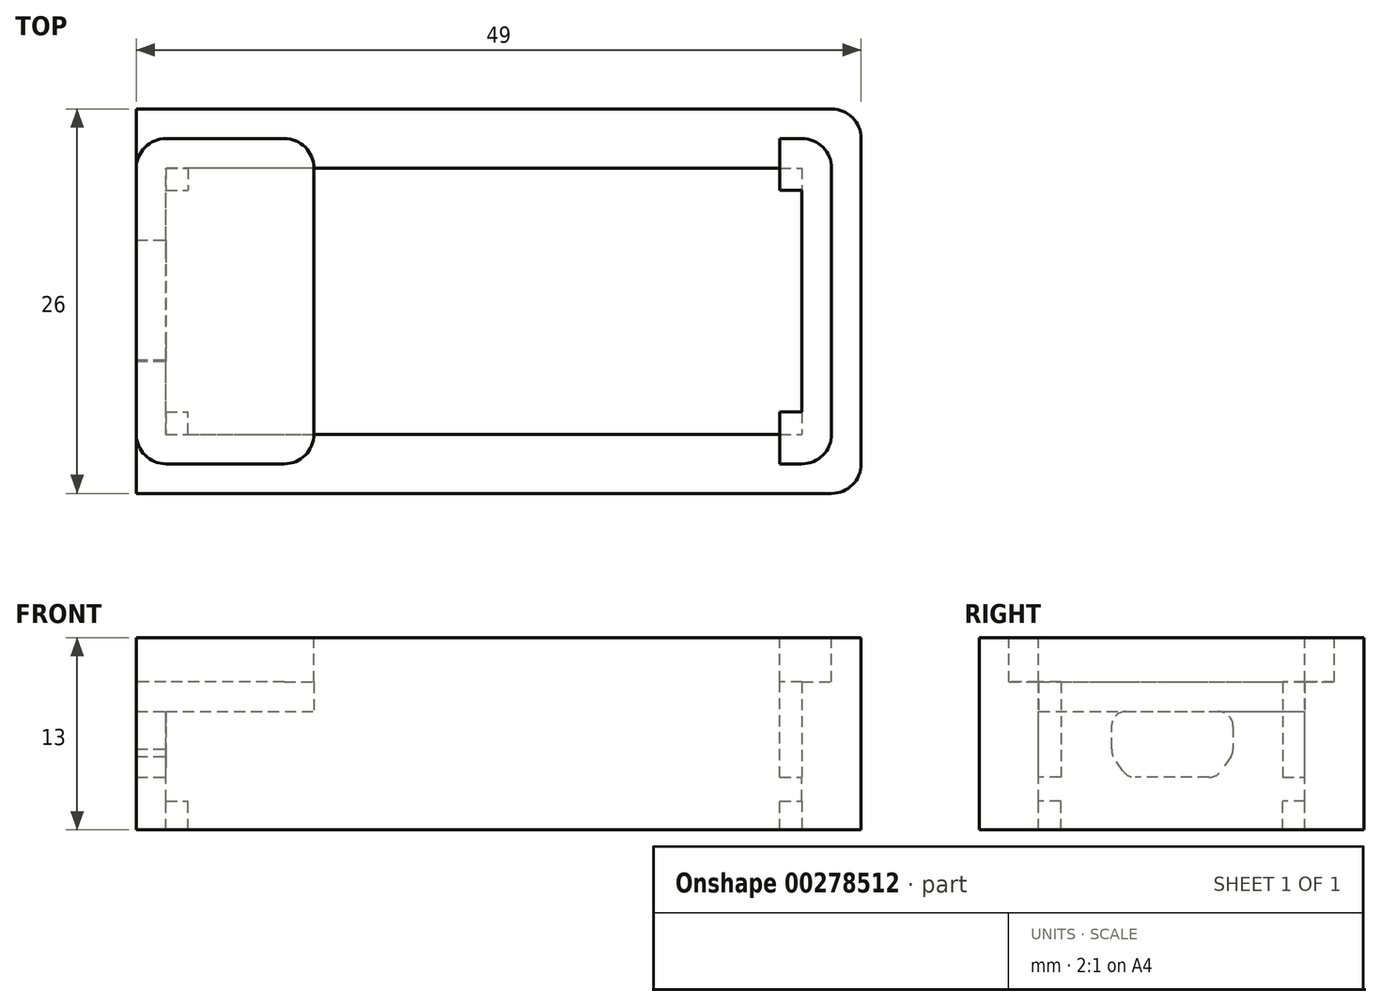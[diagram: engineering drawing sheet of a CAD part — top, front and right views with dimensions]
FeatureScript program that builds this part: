
annotation { "Feature Type Name" : "Feature", "Feature Type Description" : "" }
export const myFeature = defineFeature(function(context is Context, id is Id, definition is map)
    precondition{}
    {
        {
            var Q0;
            Q0=qCreatedBy(makeId("Top.planeOp"),FACE);
            var sketch = newSketch(context, id + "F0", { "sketchPlane" : qUnion([Q0])});
            skLineSegment(sketch, "E0.bottom", {"start": v(-21.5, 9) * mm, "end": v(21.5, 9) * mm, "construction": true});
            skLineSegment(sketch, "E0.top", {"start": v(-21.5, -9) * mm, "end": v(21.5, -9) * mm, "construction": true});
            skLineSegment(sketch, "E0.left", {"start": v(-21.5, 9) * mm, "end": v(-21.5, -9) * mm, "construction": true});
            skLineSegment(sketch, "E0.right", {"start": v(21.5, 9) * mm, "end": v(21.5, -9) * mm, "construction": true});
            skPoint(sketch, "E0.middle", {"position": v(0, 0) * mm});
            skLineSegment(sketch, "E1", {"start": v(-11.5, 15.37) * mm, "end": v(-11.5, -15.55) * mm, "construction": true});
            skLineSegment(sketch, "E2.bottom", {"start": v(-11.5, 9) * mm, "end": v(-21.5, 9) * mm});
            skLineSegment(sketch, "E2.top", {"start": v(-11.5, 11) * mm, "end": v(-21.5, 11) * mm});
            skLineSegment(sketch, "E2.left", {"start": v(-11.5, 9) * mm, "end": v(-11.5, 11) * mm});
            skLineSegment(sketch, "E2.right", {"start": v(-21.5, 9) * mm, "end": v(-21.5, 11) * mm});
            skLineSegment(sketch, "E3.bottom", {"start": v(-21.5, 9) * mm, "end": v(-11.5, 9) * mm});
            skLineSegment(sketch, "E3.top", {"start": v(-21.5, -9) * mm, "end": v(-11.5, -9) * mm});
            skLineSegment(sketch, "E3.left", {"start": v(-21.5, 9) * mm, "end": v(-21.5, -9) * mm});
            skLineSegment(sketch, "E3.right", {"start": v(-11.5, 9) * mm, "end": v(-11.5, -9) * mm});
            skLineSegment(sketch, "E4.MirrorCS", {"start": v(-21.5, -9) * mm, "end": v(-21.5, -11) * mm});
            skLineSegment(sketch, "E5.MirrorCS", {"start": v(-11.5, -11) * mm, "end": v(-21.5, -11) * mm});
            skLineSegment(sketch, "E6.MirrorCS", {"start": v(-11.5, -9) * mm, "end": v(-11.5, -11) * mm});
            skLineSegment(sketch, "E7.bottom", {"start": v(21.5, -9) * mm, "end": v(20, -9) * mm});
            skLineSegment(sketch, "E7.top", {"start": v(21.5, -11) * mm, "end": v(20, -11) * mm});
            skLineSegment(sketch, "E7.left", {"start": v(21.5, -9) * mm, "end": v(21.5, -11) * mm});
            skLineSegment(sketch, "E7.right", {"start": v(20, -9) * mm, "end": v(20, -11) * mm});
            skLineSegment(sketch, "E8.MirrorCS", {"start": v(20, 9) * mm, "end": v(20, 11) * mm});
            skLineSegment(sketch, "E9.MirrorCS", {"start": v(21.5, 11) * mm, "end": v(20, 11) * mm});
            skLineSegment(sketch, "E10.MirrorCS", {"start": v(21.5, 9) * mm, "end": v(21.5, 11) * mm});
            skLineSegment(sketch, "E11", {"start": v(21.5, 9) * mm, "end": v(20, 9) * mm});
            skLineSegment(sketch, "E12.bottom", {"start": v(21.5, -11) * mm, "end": v(23.5, -11) * mm});
            skLineSegment(sketch, "E12.top", {"start": v(21.5, 11) * mm, "end": v(23.5, 11) * mm});
            skLineSegment(sketch, "E12.left", {"start": v(21.5, -11) * mm, "end": v(21.5, 11) * mm});
            skLineSegment(sketch, "E12.right", {"start": v(23.5, -11) * mm, "end": v(23.5, 11) * mm});
            skLineSegment(sketch, "E13.bottom", {"start": v(20, -9) * mm, "end": v(21.5, -9) * mm});
            skLineSegment(sketch, "E13.top", {"start": v(20, -7.5) * mm, "end": v(21.5, -7.5) * mm});
            skLineSegment(sketch, "E13.left", {"start": v(20, -9) * mm, "end": v(20, -7.5) * mm});
            skLineSegment(sketch, "E13.right", {"start": v(21.5, -9) * mm, "end": v(21.5, -7.5) * mm});
            skLineSegment(sketch, "E14.top", {"start": v(21.5, 7.5) * mm, "end": v(20, 7.5) * mm});
            skLineSegment(sketch, "E14.left", {"start": v(21.5, 9) * mm, "end": v(21.5, 7.5) * mm});
            skLineSegment(sketch, "E14.right", {"start": v(20, 9) * mm, "end": v(20, 7.5) * mm});
            skSolve(sketch);
        }
        {
            var Q0;
            {var subQ2=sQuery(id+"F0.wireOp",EDGE,"E11");var subQ3=makeQuery(id+"F0.imprint","IMPRINT",EDGE,{"derivedFrom":subQ2});var subQ4=sQuery(id+"F0.wireOp",EDGE,"E7.left");var subQ5=makeQuery(id+"F0.imprint","IMPRINT",EDGE,{"derivedFrom":subQ4});var subQ11=sQuery(id+"F0.wireOp",EDGE,"E7.bottom");var subQ14=makeQuery(id+"F0.imprint","IMPRINT",EDGE,{"derivedFrom":subQ11});var subQ15=makeQuery(id+"F0.imprint","IMPRINT",EDGE,{"derivedFrom":sQuery(id+"F0.wireOp",EDGE,"E2.bottom")});var subQ16=makeQuery(id+"F0.imprint","IMPRINT",EDGE,{"derivedFrom":sQuery(id+"F0.wireOp",EDGE,"E3.top")});Q0=qUnion([makeQuery(id+"F0.imprint","IMPRINT",FACE,{"disambiguationData":[TD([[subQ15,-1.0]])]}),makeQuery(id+"F0.imprint","IMPRINT",FACE,{"disambiguationData":[TD([[subQ16,-1.0]])]}),makeQuery(id+"F0.imprint","IMPRINT",FACE,{"disambiguationData":[TD([[subQ15,1.0]])]}),makeQuery(id+"F0.imprint","IMPRINT",FACE,{"disambiguationData":[TD([[subQ14,1.0]])]}),makeQuery(id+"F0.imprint","IMPRINT",FACE,{"disambiguationData":[TD([[subQ3,1.0]])]}),makeQuery(id+"F0.imprint","IMPRINT",FACE,{"disambiguationData":[TD([[subQ14,-1.0]])]}),makeQuery(id+"F0.imprint","IMPRINT",FACE,{"disambiguationData":[TD([[subQ5,1.0]])]}),makeQuery(id+"F0.imprint","IMPRINT",FACE,{"disambiguationData":[TD([[makeQuery(id+"F0.imprint","IMPRINT",EDGE,{"derivedFrom":sQuery(id+"F0.wireOp",EDGE,"E8.MirrorCS")}),-1.0]])]})]);}
            extrude(context, id + "F1", {"entities" : qUnion([Q0]), "depth" : 2 * mm});
        }
        {
            var Q0;
            Q0=makeQuery(id+"F0.imprint","IMPRINT",FACE,{"disambiguationData":[TD([[makeQuery(id+"F0.imprint","IMPRINT",EDGE,{"derivedFrom":sQuery(id+"F0.wireOp",EDGE,"E2.bottom")}),-1.0]])]});
            var Q1;
            Q1=makeQuery(id+"F0.imprint","IMPRINT",FACE,{"disambiguationData":[TD([[makeQuery(id+"F0.imprint","IMPRINT",EDGE,{"derivedFrom":sQuery(id+"F0.wireOp",EDGE,"E3.top")}),-1.0]])]});
            extrude(context, id + "F2", {"entities" : qUnion([Q0, Q1]), "operationType" : NewBodyOperationType.ADD, "oppositeDirection" : true, "depth" : 8 * mm});
        }
        {
            var Q0;
            {var subQ0=sQuery(id+"F0.wireOp",EDGE,"E4.MirrorCS");var subQ1=sQuery(id+"F0.wireOp",EDGE,"E2.right");Q0=makeQuery(id+"F2.boolean.opBoolean","MERGE",FACE,{"derivedFrom":[makeQuery(id+"F1.opExtrude","SWEPT_FACE",FACE,{"disambiguationData":[OSD([subQ1,sQuery(id+"F0.wireOp",EDGE,"E3.left"),subQ0])]}),makeQuery(id+"F2.opExtrude","SWEPT_FACE",FACE,{"disambiguationData":[OSD([subQ1])]}),makeQuery(id+"F2.opExtrude","SWEPT_FACE",FACE,{"disambiguationData":[OSD([subQ0])]})]});}
            var sketch = newSketch(context, id + "F3", { "sketchPlane" : qUnion([Q0])});
            skLineSegment(sketch, "E15", {"start": v(-9, -6.04) * mm, "end": v(9, -6.04) * mm});
            skPoint(sketch, "E15.endSnap0", {"position": v(9, -4) * mm});
            skLineSegment(sketch, "E16.bottom", {"start": v(-9, -8) * mm, "end": v(-7.5, -8) * mm});
            skLineSegment(sketch, "E16.top", {"start": v(-9, -6.04) * mm, "end": v(-7.5, -6.04) * mm});
            skLineSegment(sketch, "E16.left", {"start": v(-9, -8) * mm, "end": v(-9, -6.04) * mm});
            skLineSegment(sketch, "E16.right", {"start": v(-7.5, -8) * mm, "end": v(-7.5, -6.04) * mm});
            skLineSegment(sketch, "E17.MirrorCS", {"start": v(7.5, -8) * mm, "end": v(7.5, -6.04) * mm});
            skLineSegment(sketch, "E18.MirrorCS", {"start": v(9, -8) * mm, "end": v(7.5, -8) * mm});
            skLineSegment(sketch, "E19.MirrorCS", {"start": v(9, -8) * mm, "end": v(9, -6.04) * mm});
            skArc(sketch, "E20.0.14", {"start": v(2.48, -4.24) * mm, "mid": v(2.86, -4.15) * mm, "end": v(3.15, -3.9) * mm});
            skLineSegment(sketch, "E20.0.15", {"start": v(3.15, -3.9) * mm, "end": v(3.8, -2.93) * mm});
            skArc(sketch, "E20.0.16", {"start": v(3.8, -2.93) * mm, "mid": v(3.85, -2.74) * mm, "end": v(3.85, -2.54) * mm});
            skLineSegment(sketch, "E20.0.17", {"start": v(3.85, -2.54) * mm, "end": v(3.85, -0.9) * mm});
            skArc(sketch, "E20.0.18", {"start": v(3.85, -0.9) * mm, "mid": v(3.64, -0.4) * mm, "end": v(3.15, -0.2) * mm});
            skLineSegment(sketch, "E20.0.19", {"start": v(3.15, -0.2) * mm, "end": v(-3.15, -0.2) * mm});
            skArc(sketch, "E20.0.20", {"start": v(-3.15, -0.2) * mm, "mid": v(-3.72, -0.43) * mm, "end": v(-3.95, -1) * mm});
            skLineSegment(sketch, "E20.0.21", {"start": v(-3.95, -1) * mm, "end": v(-3.95, -2.54) * mm});
            skArc(sketch, "E20.0.22", {"start": v(-3.95, -2.54) * mm, "mid": v(-3.92, -2.74) * mm, "end": v(-3.83, -2.93) * mm});
            skLineSegment(sketch, "E20.0.23", {"start": v(-3.83, -2.93) * mm, "end": v(-3.18, -3.9) * mm});
            skArc(sketch, "E20.0.24", {"start": v(-3.18, -3.9) * mm, "mid": v(-2.9, -4.15) * mm, "end": v(-2.52, -4.24) * mm});
            skLineSegment(sketch, "E21", {"start": v(-2.52, -4.24) * mm, "end": v(2.48, -4.24) * mm});
            skArc(sketch, "E22.0", {"start": v(3.97, -3.03) * mm, "mid": v(4.05, -2.78) * mm, "end": v(4.05, -2.52) * mm});
            skLineSegment(sketch, "E22.1", {"start": v(-4.15, -1) * mm, "end": v(-4.15, -2.54) * mm});
            skArc(sketch, "E22.2", {"start": v(-3.15, 0) * mm, "mid": v(-3.86, -0.3) * mm, "end": v(-4.15, -1) * mm});
            skLineSegment(sketch, "E22.3", {"start": v(3.15, 0) * mm, "end": v(-3.15, 0) * mm});
            skArc(sketch, "E22.4", {"start": v(4.05, -0.9) * mm, "mid": v(3.79, -0.26) * mm, "end": v(3.15, 0) * mm});
            skArc(sketch, "E22.5", {"start": v(-4.15, -2.54) * mm, "mid": v(-4.11, -2.8) * mm, "end": v(-4, -3.04) * mm});
            skLineSegment(sketch, "E22.6", {"start": v(4.05, -2.52) * mm, "end": v(4.05, -0.9) * mm});
            skLineSegment(sketch, "E22.7", {"start": v(-4, -3.04) * mm, "end": v(-3.35, -4) * mm});
            skArc(sketch, "E22.8", {"start": v(-3.35, -4) * mm, "mid": v(-2.99, -4.33) * mm, "end": v(-2.52, -4.44) * mm});
            skLineSegment(sketch, "E22.9", {"start": v(-2.52, -4.44) * mm, "end": v(2.48, -4.44) * mm});
            skArc(sketch, "E22.10", {"start": v(2.48, -4.44) * mm, "mid": v(2.95, -4.33) * mm, "end": v(3.31, -4) * mm});
            skLineSegment(sketch, "E22.11", {"start": v(3.31, -4) * mm, "end": v(3.97, -3.03) * mm});
            skPoint(sketch, "E23", {"position": v(0, 0) * mm});
            skLineSegment(sketch, "E24", {"start": v(7.5, -8) * mm, "end": v(-7.5, -8) * mm});
            skSolve(sketch);
        }
        {
            var Q0;
            Q0=makeQuery(id+"F3.imprint","IMPRINT",FACE,{"disambiguationData":[TD([[makeQuery(id+"F3.imprint","IMPRINT",EDGE,{"derivedFrom":sQuery(id+"F3.wireOp",EDGE,"E22.0")}),-1.0]])]});
            var Q1;
            {var subQ10=sQuery(id+"F3.wireOp",EDGE,"E16.left");Q1=makeQuery(id+"F3.imprint","IMPRINT",FACE,{"disambiguationData":[TD([[makeQuery(id+"F3.imprint","IMPRINT",EDGE,{"derivedFrom":subQ10}),1.0]])]});}
            var Q2;
            {var subQ0=sQuery(id+"F3.wireOp",EDGE,"E16.right");Q2=makeQuery(id+"F3.imprint","IMPRINT",FACE,{"disambiguationData":[TD([[makeQuery(id+"F3.imprint","IMPRINT",EDGE,{"derivedFrom":subQ0}),-1.0]])]});}
            extrude(context, id + "F4", {"entities" : qUnion([Q0, Q1, Q2]), "operationType" : NewBodyOperationType.ADD, "depth" : 2 * mm});
        }
        {
            var Q0;
            {var subQ0=sQuery(id+"F3.wireOp",EDGE,"E17.MirrorCS");Q0=makeQuery(id+"F3.imprint","IMPRINT",FACE,{"disambiguationData":[TD([[makeQuery(id+"F3.imprint","IMPRINT",EDGE,{"derivedFrom":subQ0}),-1.0]])]});}
            var Q1;
            Q1=makeQuery(id+"F3.imprint","IMPRINT",FACE,{"disambiguationData":[TD([[makeQuery(id+"F3.imprint","IMPRINT",EDGE,{"derivedFrom":sQuery(id+"F3.wireOp",EDGE,"E16.bottom")}),1.0]])]});
            var Q2;
            Q2=makeQuery(id+"F4.opExtrude","CAP_FACE",FACE,{"disambiguationData":[OSD([sQuery(id+"F0.wireOp",EDGE,"E2.top"),sQuery(id+"F0.wireOp",EDGE,"E2.right"),sQuery(id+"F0.wireOp",EDGE,"E3.left"),sQuery(id+"F0.wireOp",EDGE,"E4.MirrorCS"),sQuery(id+"F0.wireOp",EDGE,"E5.MirrorCS"),sQuery(id+"F3.wireOp",EDGE,"E15"),sQuery(id+"F3.wireOp",EDGE,"E16.left"),sQuery(id+"F3.wireOp",EDGE,"E16.right"),sQuery(id+"F3.wireOp",EDGE,"E17.MirrorCS"),sQuery(id+"F3.wireOp",EDGE,"E19.MirrorCS"),sQuery(id+"F3.wireOp",EDGE,"E22.0"),sQuery(id+"F3.wireOp",EDGE,"E22.1"),sQuery(id+"F3.wireOp",EDGE,"E22.2"),sQuery(id+"F3.wireOp",EDGE,"E22.3"),sQuery(id+"F3.wireOp",EDGE,"E22.4"),sQuery(id+"F3.wireOp",EDGE,"E22.5"),sQuery(id+"F3.wireOp",EDGE,"E22.6"),sQuery(id+"F3.wireOp",EDGE,"E22.7"),sQuery(id+"F3.wireOp",EDGE,"E22.8"),sQuery(id+"F3.wireOp",EDGE,"E22.9"),sQuery(id+"F3.wireOp",EDGE,"E22.10"),sQuery(id+"F3.wireOp",EDGE,"E22.11"),sQuery(id+"F3.wireOp",EDGE,"E24")])],"isStart":false});
            extrude(context, id + "F5", {"entities" : qUnion([Q0, Q1]), "operationType" : NewBodyOperationType.ADD, "endBound" : BoundingType.UP_TO_SURFACE, "endBoundEntityFace" : qUnion([Q2]), "depth" : 3.5 * mm, "hasSecondDirection" : true, "secondDirectionOppositeDirection" : true, "secondDirectionDepth" : 1.5 * mm});
        }
        {
            var Q0;
            {var subQ1=sQuery(id+"F0.wireOp",EDGE,"E7.left");Q0=makeQuery(id+"F0.imprint","IMPRINT",FACE,{"disambiguationData":[TD([[makeQuery(id+"F0.imprint","IMPRINT",EDGE,{"derivedFrom":subQ1}),1.0]])]});}
            var Q1;
            Q1=makeQuery(id+"F0.imprint","IMPRINT",FACE,{"disambiguationData":[TD([[makeQuery(id+"F0.imprint","IMPRINT",EDGE,{"derivedFrom":sQuery(id+"F0.wireOp",EDGE,"E7.bottom")}),1.0]])]});
            var Q2;
            Q2=makeQuery(id+"F0.imprint","IMPRINT",FACE,{"disambiguationData":[TD([[makeQuery(id+"F0.imprint","IMPRINT",EDGE,{"derivedFrom":sQuery(id+"F0.wireOp",EDGE,"E8.MirrorCS")}),-1.0]])]});
            var Q3;
            {var subQ0=sQuery(id+"F0.wireOp",EDGE,"E7.bottom");Q3=makeQuery(id+"F0.imprint","IMPRINT",FACE,{"disambiguationData":[TD([[makeQuery(id+"F0.imprint","IMPRINT",EDGE,{"derivedFrom":subQ0}),-1.0]])]});}
            var Q4;
            {var subQ0=sQuery(id+"F0.wireOp",EDGE,"E11");Q4=makeQuery(id+"F0.imprint","IMPRINT",FACE,{"disambiguationData":[TD([[makeQuery(id+"F0.imprint","IMPRINT",EDGE,{"derivedFrom":subQ0}),1.0]])]});}
            var Q5;
            {var subQ0=sQuery(id+"F0.wireOp",EDGE,"E4.MirrorCS");var subQ1=sQuery(id+"F0.wireOp",EDGE,"E2.right");Q5=makeQuery(id+"F5.boolean.opBoolean","MERGE",FACE,{"derivedFrom":[makeQuery(id+"F4.opExtrude","SWEPT_FACE",FACE,{"disambiguationData":[OSD([sQuery(id+"F3.wireOp",EDGE,"E24")])]}),makeQuery(id+"F4.boolean.opBoolean","MERGE",FACE,{"derivedFrom":[makeQuery(id+"F2.opExtrude","CAP_FACE",FACE,{"disambiguationData":[OSD([sQuery(id+"F0.wireOp",EDGE,"E2.bottom"),sQuery(id+"F0.wireOp",EDGE,"E2.top"),sQuery(id+"F0.wireOp",EDGE,"E2.left"),subQ1])],"isStart":false}),makeQuery(id+"F4.opExtrude","SWEPT_FACE",FACE,{"disambiguationData":[OSD([subQ1])]})]}),makeQuery(id+"F4.boolean.opBoolean","MERGE",FACE,{"derivedFrom":[makeQuery(id+"F2.opExtrude","CAP_FACE",FACE,{"disambiguationData":[OSD([sQuery(id+"F0.wireOp",EDGE,"E3.top"),subQ0,sQuery(id+"F0.wireOp",EDGE,"E5.MirrorCS"),sQuery(id+"F0.wireOp",EDGE,"E6.MirrorCS")])],"isStart":false}),makeQuery(id+"F4.opExtrude","SWEPT_FACE",FACE,{"disambiguationData":[OSD([subQ0])]})]}),makeQuery(id+"F5.opExtrude","SWEPT_FACE",FACE,{"disambiguationData":[OSD([sQuery(id+"F3.wireOp",EDGE,"E16.bottom")])]}),makeQuery(id+"F5.opExtrude","SWEPT_FACE",FACE,{"disambiguationData":[OSD([sQuery(id+"F3.wireOp",EDGE,"E18.MirrorCS")])]})]});}
            extrude(context, id + "F6", {"entities" : qUnion([Q0, Q1, Q2, Q3, Q4]), "operationType" : NewBodyOperationType.ADD, "endBound" : BoundingType.UP_TO_SURFACE, "oppositeDirection" : true, "endBoundEntityFace" : qUnion([Q5]), "depth" : 25 * mm});
        }
        {
            var Q0;
            {var subQ0=sQuery(id+"F0.wireOp",EDGE,"E7.bottom");Q0=makeQuery(id+"F0.imprint","IMPRINT",FACE,{"disambiguationData":[TD([[makeQuery(id+"F0.imprint","IMPRINT",EDGE,{"derivedFrom":subQ0}),-1.0]])]});}
            var Q1;
            {var subQ0=sQuery(id+"F0.wireOp",EDGE,"E11");Q1=makeQuery(id+"F0.imprint","IMPRINT",FACE,{"disambiguationData":[TD([[makeQuery(id+"F0.imprint","IMPRINT",EDGE,{"derivedFrom":subQ0}),1.0]])]});}
            var Q2;
            {var subQ0=sQuery(id+"F3.wireOp",EDGE,"E15");Q2=makeQuery(id+"F5.opExtrude","SWEPT_FACE",FACE,{"disambiguationData":[OSD([subQ0]),TDD([makeQuery(id+"F3.imprint","IMPRINT",EDGE,{"disambiguationData":[TD([[makeQuery(id+"F3.imprint","INTERSECT",VERTEX,{"derivedFrom":[subQ0,sQuery(id+"F3.wireOp",EDGE,"E17.MirrorCS")]}),-1.0]])],"derivedFrom":subQ0})])]});}
            var Q3;
            Q3=makeQuery(id+"F4.opExtrude","SWEPT_FACE",FACE,{"disambiguationData":[OSD([sQuery(id+"F3.wireOp",EDGE,"E22.9")])]});
            extrude(context, id + "F7", {"entities" : qUnion([Q0, Q1]), "operationType" : NewBodyOperationType.REMOVE, "endBound" : BoundingType.UP_TO_SURFACE, "oppositeDirection" : true, "endBoundEntityFace" : qUnion([Q2]), "depth" : 25 * mm, "hasSecondDirection" : true, "secondDirectionBound" : SecondDirectionBoundingType.UP_TO_SURFACE, "secondDirectionOppositeDirection" : true, "secondDirectionBoundEntityFace" : qUnion([Q3]), "secondDirectionDepth" : 3.8 * mm});
        }
        {
            var Q0;
            Q0=makeQuery(id+"F4.opExtrude","CAP_EDGE",EDGE,{"disambiguationData":[OSD([sQuery(id+"F0.wireOp",EDGE,"E2.top"),sQuery(id+"F0.wireOp",EDGE,"E2.right")])],"isStart":false});
            var Q1;
            Q1=makeQuery(id+"F4.opExtrude","CAP_EDGE",EDGE,{"disambiguationData":[OSD([sQuery(id+"F0.wireOp",EDGE,"E4.MirrorCS"),sQuery(id+"F0.wireOp",EDGE,"E5.MirrorCS")])],"isStart":false});
            var Q2;
            {var subQ0=sQuery(id+"F0.wireOp",EDGE,"E2.left");var subQ1=sQuery(id+"F0.wireOp",EDGE,"E2.top");Q2=makeQuery(id+"F2.boolean.opBoolean","MERGE",EDGE,{"derivedFrom":[makeQuery(id+"F1.opExtrude","SWEPT_EDGE",EDGE,{"disambiguationData":[OSD([subQ1,subQ0])]}),makeQuery(id+"F2.opExtrude","SWEPT_EDGE",EDGE,{"disambiguationData":[OSD([subQ1,subQ0])]})]});}
            var Q3;
            {var subQ0=sQuery(id+"F0.wireOp",EDGE,"E6.MirrorCS");var subQ1=sQuery(id+"F0.wireOp",EDGE,"E5.MirrorCS");Q3=makeQuery(id+"F2.boolean.opBoolean","MERGE",EDGE,{"derivedFrom":[makeQuery(id+"F1.opExtrude","SWEPT_EDGE",EDGE,{"disambiguationData":[OSD([subQ1,subQ0])]}),makeQuery(id+"F2.opExtrude","SWEPT_EDGE",EDGE,{"disambiguationData":[OSD([subQ1,subQ0])]})]});}
            var Q4;
            {var subQ0=sQuery(id+"F0.wireOp",EDGE,"E12.right");var subQ1=sQuery(id+"F0.wireOp",EDGE,"E12.top");Q4=makeQuery(id+"F6.boolean.opBoolean","MERGE",EDGE,{"derivedFrom":[makeQuery(id+"F1.opExtrude","SWEPT_EDGE",EDGE,{"disambiguationData":[OSD([subQ1,subQ0])]}),makeQuery(id+"F6.opExtrude","SWEPT_EDGE",EDGE,{"disambiguationData":[OSD([subQ1,subQ0])]})]});}
            var Q5;
            {var subQ0=sQuery(id+"F0.wireOp",EDGE,"E12.right");var subQ1=sQuery(id+"F0.wireOp",EDGE,"E12.bottom");Q5=makeQuery(id+"F6.boolean.opBoolean","MERGE",EDGE,{"derivedFrom":[makeQuery(id+"F1.opExtrude","SWEPT_EDGE",EDGE,{"disambiguationData":[OSD([subQ1,subQ0])]}),makeQuery(id+"F6.opExtrude","SWEPT_EDGE",EDGE,{"disambiguationData":[OSD([subQ1,subQ0])]})]});}
            fillet(context, id + "F8", {"entities" : qUnion([Q0, Q1, Q2, Q3, Q4, Q5]), "radius" : 2 * mm, "tangentPropagation" : true, "allowEdgeOverflow" : false});
        }
        {
            var Q0;
            {var subQ0=sQuery(id+"F0.wireOp",EDGE,"E4.MirrorCS");var subQ1=sQuery(id+"F0.wireOp",EDGE,"E3.left");var subQ2=sQuery(id+"F0.wireOp",EDGE,"E2.right");Q0=makeQuery(id+"F4.boolean.opBoolean","MERGE",FACE,{"derivedFrom":[makeQuery(id+"F1.opExtrude","CAP_FACE",FACE,{"disambiguationData":[OSD([sQuery(id+"F0.wireOp",EDGE,"E2.top"),sQuery(id+"F0.wireOp",EDGE,"E2.left"),subQ2,subQ1,sQuery(id+"F0.wireOp",EDGE,"E3.right"),subQ0,sQuery(id+"F0.wireOp",EDGE,"E5.MirrorCS"),sQuery(id+"F0.wireOp",EDGE,"E6.MirrorCS")])],"isStart":false}),makeQuery(id+"F4.opExtrude","SWEPT_FACE",FACE,{"disambiguationData":[OSD([subQ2,subQ1,subQ0])]})]});}
            var sketch = newSketch(context, id + "F9", { "sketchPlane" : qUnion([Q0])});
            skPoint(sketch, "E25.0", {"position": v(23.5, -11) * mm});
            skPoint(sketch, "E26.0", {"position": v(23.5, 11) * mm});
            skPoint(sketch, "E27.0", {"position": v(-23.5, 0) * mm});
            skArc(sketch, "E28.0", {"start": v(-23.5, -9) * mm, "mid": v(-22.91, -10.41) * mm, "end": v(-21.5, -11) * mm});
            skArc(sketch, "E29.0", {"start": v(-21.5, 11) * mm, "mid": v(-22.91, 10.41) * mm, "end": v(-23.5, 9) * mm});
            skArc(sketch, "E30.0", {"start": v(21.5, -11) * mm, "mid": v(22.91, -10.41) * mm, "end": v(23.5, -9) * mm});
            skArc(sketch, "E31.0", {"start": v(23.5, 9) * mm, "mid": v(22.91, 10.41) * mm, "end": v(21.5, 11) * mm});
            skLineSegment(sketch, "E32", {"start": v(-23.5, -9) * mm, "end": v(-23.5, -13) * mm});
            skLineSegment(sketch, "E33", {"start": v(-23.5, -13) * mm, "end": v(23.5, -13) * mm});
            skLineSegment(sketch, "E34", {"start": v(25.5, -11) * mm, "end": v(25.5, 0) * mm});
            skPoint(sketch, "E35.visualSharp", {"position": v(25.5, -13) * mm});
            skArc(sketch, "E35.filletArc", {"start": v(23.5, -13) * mm, "mid": v(24.91, -12.41) * mm, "end": v(25.5, -11) * mm});
            skLineSegment(sketch, "E36", {"start": v(23.5, -9) * mm, "end": v(23.5, 0) * mm});
            skLineSegment(sketch, "E37", {"start": v(21.5, -11) * mm, "end": v(-21.5, -11) * mm});
            skLineSegment(sketch, "E38.MirrorCS", {"start": v(25.5, 11) * mm, "end": v(25.5, 0) * mm});
            skArc(sketch, "E39.MirrorCS", {"start": v(23.5, 13) * mm, "mid": v(24.91, 12.41) * mm, "end": v(25.5, 11) * mm});
            skLineSegment(sketch, "E40.MirrorCS", {"start": v(-23.5, 13) * mm, "end": v(23.5, 13) * mm});
            skLineSegment(sketch, "E41.MirrorCS", {"start": v(-23.5, 9) * mm, "end": v(-23.5, 13) * mm});
            skArc(sketch, "E42.MirrorCS", {"start": v(-23.5, 9) * mm, "mid": v(-22.91, 10.41) * mm, "end": v(-21.5, 11) * mm});
            skLineSegment(sketch, "E43.MirrorCS", {"start": v(21.5, 11) * mm, "end": v(-21.5, 11) * mm});
            skLineSegment(sketch, "E44.MirrorCS", {"start": v(23.5, 9) * mm, "end": v(23.5, 0) * mm});
            skLineSegment(sketch, "E45", {"start": v(-23.5, -9) * mm, "end": v(-23.5, 9) * mm});
            skLineSegment(sketch, "E46.0.0", {"start": v(-13.5, 11) * mm, "end": v(-21.5, 11) * mm});
            skLineSegment(sketch, "E46.0.2", {"start": v(-23.5, 9) * mm, "end": v(-23.5, -9) * mm});
            skLineSegment(sketch, "E46.0.4", {"start": v(-21.5, -11) * mm, "end": v(-13.5, -11) * mm});
            skArc(sketch, "E46.0.5", {"start": v(-13.5, -11) * mm, "mid": v(-12.09, -10.41) * mm, "end": v(-11.5, -9) * mm});
            skLineSegment(sketch, "E46.0.6", {"start": v(-11.5, -9) * mm, "end": v(-11.5, 9) * mm});
            skArc(sketch, "E46.0.7", {"start": v(-11.5, 9) * mm, "mid": v(-12.09, 10.41) * mm, "end": v(-13.5, 11) * mm});
            skLineSegment(sketch, "E47.0.0", {"start": v(20, -11) * mm, "end": v(21.5, -11) * mm});
            skLineSegment(sketch, "E47.0.2", {"start": v(23.5, -9) * mm, "end": v(23.5, 9) * mm});
            skLineSegment(sketch, "E47.0.4", {"start": v(21.5, 11) * mm, "end": v(20, 11) * mm});
            skLineSegment(sketch, "E47.0.5", {"start": v(20, 11) * mm, "end": v(20, 7.5) * mm});
            skLineSegment(sketch, "E47.0.6", {"start": v(20, 7.5) * mm, "end": v(21.5, 7.5) * mm});
            skLineSegment(sketch, "E47.0.7", {"start": v(21.5, 7.5) * mm, "end": v(21.5, -7.5) * mm});
            skLineSegment(sketch, "E47.0.8", {"start": v(21.5, -7.5) * mm, "end": v(20, -7.5) * mm});
            skLineSegment(sketch, "E47.0.9", {"start": v(20, -7.5) * mm, "end": v(20, -11) * mm});
            skPoint(sketch, "E48.0", {"position": v(20, -9) * mm});
            skPoint(sketch, "E49.0", {"position": v(20, 9) * mm});
            skLineSegment(sketch, "E50", {"start": v(20, -9) * mm, "end": v(-11.5, -9) * mm});
            skLineSegment(sketch, "E51.MirrorCS", {"start": v(20, 9) * mm, "end": v(-11.5, 9) * mm});
            skSolve(sketch);
        }
        {
            var Q0;
            Q0=makeQuery(id+"F9.imprint","IMPRINT",FACE,{"disambiguationData":[TD([[makeQuery(id+"F9.imprint","IMPRINT",EDGE,{"derivedFrom":sQuery(id+"F9.wireOp",EDGE,"E32")}),1.0]])]});
            var Q1;
            {var subQ0=sQuery(id+"F9.wireOp",EDGE,"E37");Q1=makeQuery(id+"F9.imprint","IMPRINT",FACE,{"disambiguationData":[TD([[makeQuery(id+"F9.imprint","IMPRINT",EDGE,{"derivedFrom":subQ0}),-1.0]])]});}
            var Q2;
            {var subQ0=sQuery(id+"F9.wireOp",EDGE,"E43.MirrorCS");Q2=makeQuery(id+"F9.imprint","IMPRINT",FACE,{"disambiguationData":[TD([[makeQuery(id+"F9.imprint","IMPRINT",EDGE,{"derivedFrom":subQ0}),1.0]])]});}
            var Q3;
            Q3=makeQuery(id+"F6.opExtrude","CAP_FACE",FACE,{"disambiguationData":[OSD([sQuery(id+"F0.wireOp",EDGE,"E7.top"),sQuery(id+"F0.wireOp",EDGE,"E7.right"),sQuery(id+"F0.wireOp",EDGE,"E8.MirrorCS"),sQuery(id+"F0.wireOp",EDGE,"E9.MirrorCS"),sQuery(id+"F0.wireOp",EDGE,"E12.bottom"),sQuery(id+"F0.wireOp",EDGE,"E12.top"),sQuery(id+"F0.wireOp",EDGE,"E12.left"),sQuery(id+"F0.wireOp",EDGE,"E12.right"),sQuery(id+"F0.wireOp",EDGE,"E13.top"),sQuery(id+"F0.wireOp",EDGE,"E13.left"),sQuery(id+"F0.wireOp",EDGE,"E14.top"),sQuery(id+"F0.wireOp",EDGE,"E14.right")])],"isStart":false});
            extrude(context, id + "F10", {"entities" : qUnion([Q0, Q1, Q2]), "endBound" : BoundingType.UP_TO_SURFACE, "oppositeDirection" : true, "endBoundEntityFace" : qUnion([Q3]), "depth" : 5 * mm});
        }
        {
            var Q0;
            Q0=makeQuery(id+"F9.imprint","IMPRINT",FACE,{"disambiguationData":[TD([[makeQuery(id+"F9.imprint","IMPRINT",EDGE,{"derivedFrom":sQuery(id+"F9.wireOp",EDGE,"E32")}),1.0]])]});
            var Q1;
            Q1=makeQuery(id+"F9.imprint","IMPRINT",FACE,{"disambiguationData":[TD([[makeQuery(id+"F9.imprint","IMPRINT",EDGE,{"derivedFrom":sQuery(id+"F9.wireOp",EDGE,"E47.0.0")}),1.0]])]});
            var Q2;
            Q2=makeQuery(id+"F9.imprint","IMPRINT",FACE,{"disambiguationData":[TD([[makeQuery(id+"F9.imprint","IMPRINT",EDGE,{"derivedFrom":sQuery(id+"F9.wireOp",EDGE,"E46.0.0")}),1.0]])]});
            var Q3;
            {var subQ0=sQuery(id+"F9.wireOp",EDGE,"E43.MirrorCS");Q3=makeQuery(id+"F9.imprint","IMPRINT",FACE,{"disambiguationData":[TD([[makeQuery(id+"F9.imprint","IMPRINT",EDGE,{"derivedFrom":subQ0}),1.0]])]});}
            var Q4;
            {var subQ0=sQuery(id+"F9.wireOp",EDGE,"E37");Q4=makeQuery(id+"F9.imprint","IMPRINT",FACE,{"disambiguationData":[TD([[makeQuery(id+"F9.imprint","IMPRINT",EDGE,{"derivedFrom":subQ0}),-1.0]])]});}
            extrude(context, id + "F11", {"entities" : qUnion([Q0, Q1, Q2, Q3, Q4]), "operationType" : NewBodyOperationType.ADD, "depth" : 3 * mm});
        }
    });
